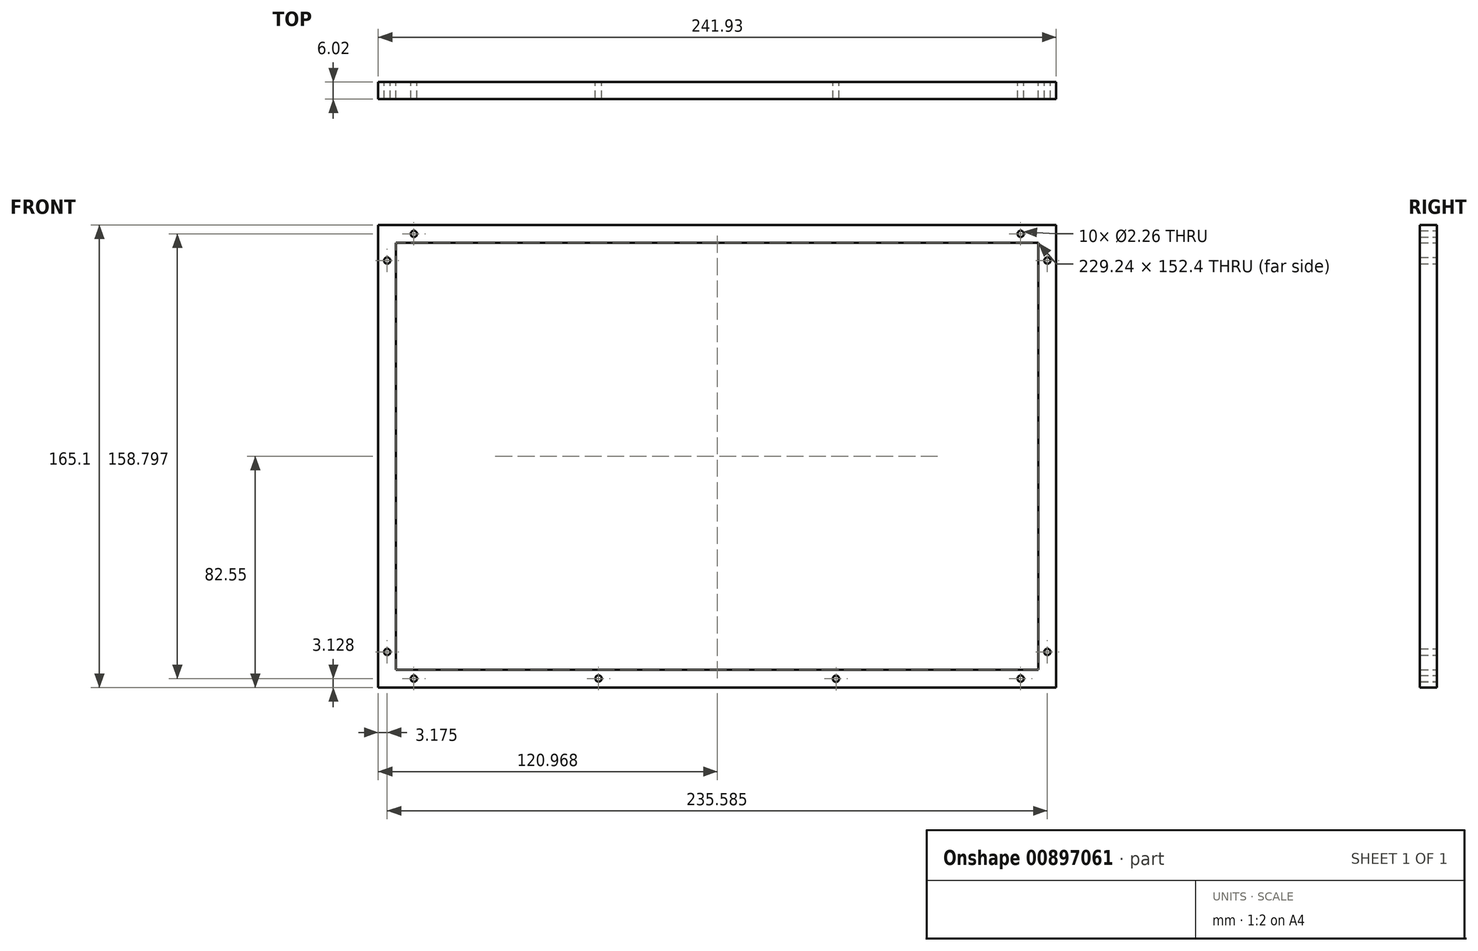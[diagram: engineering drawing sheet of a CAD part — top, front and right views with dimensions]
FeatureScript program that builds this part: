
annotation { "Feature Type Name" : "Feature", "Feature Type Description" : "" }
export const myFeature = defineFeature(function(context is Context, id is Id, definition is map)
    precondition{}
    {
        {
            var Q0;
            Q0=qCreatedBy(makeId("Front.planeOp"),FACE);
            var sketch = newSketch(context, id + "F0", { "sketchPlane" : qUnion([Q0])});
            skLineSegment(sketch, "E0.bottom", {"start": v(0, 0) * mm, "end": v(229.24, 0) * mm});
            skLineSegment(sketch, "E0.top", {"start": v(0, 152.4) * mm, "end": v(229.23, 152.4) * mm});
            skLineSegment(sketch, "E0.left", {"start": v(0, 0) * mm, "end": v(0, 152.4) * mm});
            skLineSegment(sketch, "E0.right", {"start": v(229.24, 0) * mm, "end": v(229.23, 152.4) * mm});
            skLineSegment(sketch, "E1.bottom", {"start": v(-6.35, -6.35) * mm, "end": v(235.59, -6.35) * mm});
            skLineSegment(sketch, "E1.top", {"start": v(-6.35, 158.75) * mm, "end": v(235.58, 158.75) * mm});
            skLineSegment(sketch, "E1.left", {"start": v(-6.35, -6.35) * mm, "end": v(-6.35, 158.75) * mm});
            skLineSegment(sketch, "E1.right", {"start": v(235.59, -6.35) * mm, "end": v(235.58, 158.75) * mm});
            skCircle(sketch, "E2", {"center": v(-3.17, 6.35) * mm, "radius": 1.13 * mm});
            skCircle(sketch, "E3", {"center": v(6.35, -3.18) * mm, "radius": 1.13 * mm});
            skPoint(sketch, "E4", {"position": v(0, 76.2) * mm});
            skPoint(sketch, "E5", {"position": v(229.23, 76.2) * mm});
            skLineSegment(sketch, "E6", {"start": v(0, 76.2) * mm, "end": v(229.23, 76.2) * mm, "construction": true});
            skPoint(sketch, "E7", {"position": v(114.62, 152.4) * mm});
            skPoint(sketch, "E8", {"position": v(114.62, 0) * mm});
            skLineSegment(sketch, "E9", {"start": v(114.62, 0) * mm, "end": v(114.62, 152.4) * mm, "construction": true});
            skCircle(sketch, "E10.MirrorC", {"center": v(6.35, 155.58) * mm, "radius": 1.13 * mm});
            skCircle(sketch, "E11.MirrorC", {"center": v(-3.17, 146.05) * mm, "radius": 1.13 * mm});
            skCircle(sketch, "E12.MirrorC", {"center": v(222.88, -3.18) * mm, "radius": 1.13 * mm});
            skCircle(sketch, "E13.MirrorC", {"center": v(232.4, 6.35) * mm, "radius": 1.13 * mm});
            skCircle(sketch, "E14.MirrorC", {"center": v(232.4, 146.05) * mm, "radius": 1.13 * mm});
            skCircle(sketch, "E15.MirrorC", {"center": v(222.88, 155.58) * mm, "radius": 1.13 * mm});
            skCircle(sketch, "E16", {"center": v(72.25, -3.13) * mm, "radius": 1.13 * mm});
            skCircle(sketch, "E17", {"center": v(156.98, -3.22) * mm, "radius": 1.13 * mm});
            skLineSegment(sketch, "E18", {"start": v(72.25, -3.13) * mm, "end": v(156.98, -3.22) * mm, "construction": true});
            skPoint(sketch, "E19", {"position": v(114.62, -3.18) * mm});
            skSolve(sketch);
        }
        {
            var Q0;
            Q0 = qSketchRegion(id + "F0", true);
            extrude(context, id + "F1", {"entities" : qUnion([Q0]), "depth" : 6.02 * mm, "offsetDistance" : 25.4 * mm});
        }
    });
